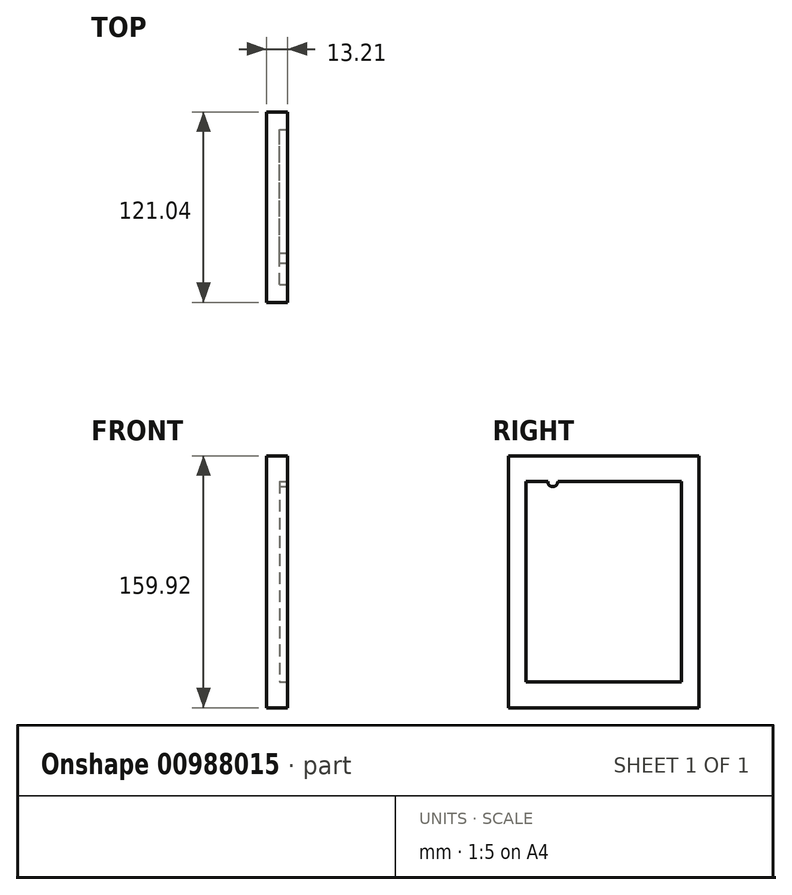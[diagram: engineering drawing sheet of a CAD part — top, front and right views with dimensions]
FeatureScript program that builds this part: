
annotation { "Feature Type Name" : "Feature", "Feature Type Description" : "" }
export const myFeature = defineFeature(function(context is Context, id is Id, definition is map)
    precondition{}
    {
        {
            var Q0;
            Q0=qCreatedBy(makeId("Right.planeOp"),FACE);
            var sketch = newSketch(context, id + "F0", { "sketchPlane" : qUnion([Q0])});
            skLineSegment(sketch, "E0.bottom", {"start": v(-48.2, 115.66) * mm, "end": v(72.84, 115.66) * mm});
            skLineSegment(sketch, "E0.top", {"start": v(-48.2, -44.26) * mm, "end": v(72.84, -44.26) * mm});
            skLineSegment(sketch, "E0.left", {"start": v(-48.2, 115.66) * mm, "end": v(-48.2, -44.26) * mm});
            skLineSegment(sketch, "E0.right", {"start": v(72.84, 115.66) * mm, "end": v(72.84, -44.26) * mm});
            skSolve(sketch);
        }
        {
            var Q0;
            Q0=makeQuery(id+"F0.imprint","IMPRINT",FACE,{"disambiguationData":[TD([[makeQuery(id+"F0.imprint","IMPRINT",EDGE,{"derivedFrom":sQuery(id+"F0.wireOp",EDGE,"E0.bottom")}),-1.0]])]});
            extrude(context, id + "F1", {"entities" : qUnion([Q0]), "depth" : 13.2 * mm, "offsetDistance" : 25.4 * mm});
        }
        {
            var Q0;
            Q0=makeQuery(id+"F1.opExtrude","CAP_FACE",FACE,{"disambiguationData":[OSD([sQuery(id+"F0.wireOp",EDGE,"E0.bottom"),sQuery(id+"F0.wireOp",EDGE,"E0.top"),sQuery(id+"F0.wireOp",EDGE,"E0.left"),sQuery(id+"F0.wireOp",EDGE,"E0.right")])],"isStart":false});
            var sketch = newSketch(context, id + "F2", { "sketchPlane" : qUnion([Q0])});
            skLineSegment(sketch, "E1.bottom", {"start": v(-48.2, 115.66) * mm, "end": v(72.84, 115.66) * mm});
            skLineSegment(sketch, "E1.top", {"start": v(-48.2, -44.26) * mm, "end": v(72.84, -44.26) * mm});
            skLineSegment(sketch, "E1.left", {"start": v(-48.2, 115.66) * mm, "end": v(-48.2, -44.26) * mm});
            skLineSegment(sketch, "E1.right", {"start": v(72.84, 115.66) * mm, "end": v(72.84, -44.26) * mm});
            skLineSegment(sketch, "E2.bottom", {"start": v(-36.98, 99.3) * mm, "end": v(61.62, 99.3) * mm});
            skLineSegment(sketch, "E2.top", {"start": v(-36.98, -27.75) * mm, "end": v(61.62, -27.75) * mm});
            skLineSegment(sketch, "E2.left", {"start": v(-36.98, 99.3) * mm, "end": v(-36.98, -27.75) * mm});
            skLineSegment(sketch, "E2.right", {"start": v(61.62, 99.3) * mm, "end": v(61.62, -27.75) * mm});
            skCircle(sketch, "E3", {"center": v(-19.95, 99.3) * mm, "radius": 3.18 * mm});
            skSolve(sketch);
        }
        {
            var Q0;
            Q0=makeQuery(id+"F2.imprint","IMPRINT",FACE,{"disambiguationData":[TD([[makeQuery(id+"F2.imprint","IMPRINT",EDGE,{"derivedFrom":sQuery(id+"F2.wireOp",EDGE,"E2.bottom")}),-1.0]])]});
            extrude(context, id + "F3", {"entities" : qUnion([Q0]), "operationType" : NewBodyOperationType.REMOVE, "oppositeDirection" : true, "depth" : 5.08 * mm, "offsetDistance" : 25.4 * mm});
        }
    });
